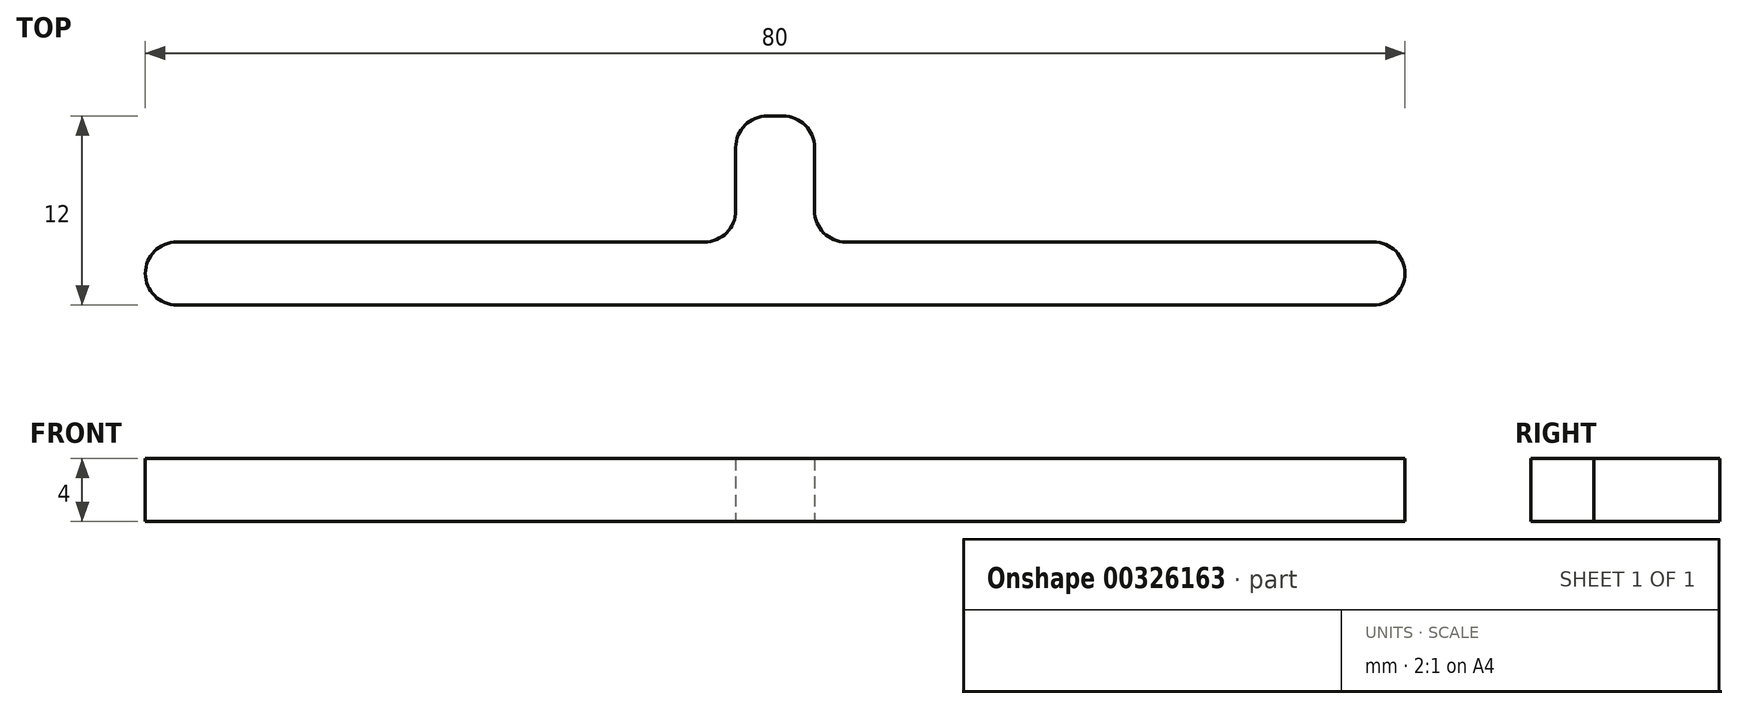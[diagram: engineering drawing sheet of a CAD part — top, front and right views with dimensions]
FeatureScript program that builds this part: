
annotation { "Feature Type Name" : "Feature", "Feature Type Description" : "" }
export const myFeature = defineFeature(function(context is Context, id is Id, definition is map)
    precondition{}
    {
        {
            var Q0;
            Q0=qCreatedBy(makeId("Top.planeOp"),FACE);
            var sketch = newSketch(context, id + "F0", { "sketchPlane" : qUnion([Q0])});
            skLineSegment(sketch, "E0.bottom", {"start": v(-40, 2) * mm, "end": v(40, 2) * mm});
            skLineSegment(sketch, "E0.top", {"start": v(-40, -2) * mm, "end": v(40, -2) * mm});
            skLineSegment(sketch, "E0.left", {"start": v(-40, 2) * mm, "end": v(-40, -2) * mm});
            skLineSegment(sketch, "E0.right", {"start": v(40, 2) * mm, "end": v(40, -2) * mm});
            skPoint(sketch, "E0.middle", {"position": v(0, 0) * mm});
            skLineSegment(sketch, "E1.bottom", {"start": v(-2.5, 2) * mm, "end": v(2.5, 2) * mm});
            skLineSegment(sketch, "E1.top", {"start": v(-2.5, 10) * mm, "end": v(2.5, 10) * mm});
            skLineSegment(sketch, "E1.left", {"start": v(-2.5, 2) * mm, "end": v(-2.5, 10) * mm});
            skLineSegment(sketch, "E1.right", {"start": v(2.5, 2) * mm, "end": v(2.5, 10) * mm});
            skPoint(sketch, "E1.middle", {"position": v(0, 6) * mm});
            skSolve(sketch);
        }
        {
            var Q0;
            Q0 = qSketchRegion(id + "F0", true);
            extrude(context, id + "F1", {"entities" : qUnion([Q0]), "depth" : 4 * mm});
        }
        {
            var Q0;
            Q0=makeQuery(id+"F1.opExtrude","SWEPT_EDGE",EDGE,{"disambiguationData":[OSD([sQuery(id+"F0.wireOp",EDGE,"E0.top"),sQuery(id+"F0.wireOp",EDGE,"E0.left")])]});
            var Q1;
            Q1=makeQuery(id+"F1.opExtrude","SWEPT_EDGE",EDGE,{"disambiguationData":[OSD([sQuery(id+"F0.wireOp",EDGE,"E0.top"),sQuery(id+"F0.wireOp",EDGE,"E0.right")])]});
            var Q2;
            Q2=makeQuery(id+"F1.opExtrude","SWEPT_EDGE",EDGE,{"disambiguationData":[OSD([sQuery(id+"F0.wireOp",EDGE,"E0.bottom"),sQuery(id+"F0.wireOp",EDGE,"E0.right")])]});
            var Q3;
            Q3=makeQuery(id+"F1.opExtrude","SWEPT_EDGE",EDGE,{"disambiguationData":[OSD([sQuery(id+"F0.wireOp",EDGE,"E0.bottom"),sQuery(id+"F0.wireOp",EDGE,"E0.left")])]});
            var Q4;
            Q4=makeQuery(id+"F1.opExtrude","SWEPT_EDGE",EDGE,{"disambiguationData":[OSD([sQuery(id+"F0.wireOp",EDGE,"E1.top"),sQuery(id+"F0.wireOp",EDGE,"E1.left")])]});
            var Q5;
            Q5=makeQuery(id+"F1.opExtrude","SWEPT_EDGE",EDGE,{"disambiguationData":[OSD([sQuery(id+"F0.wireOp",EDGE,"E1.top"),sQuery(id+"F0.wireOp",EDGE,"E1.right")])]});
            var Q6;
            Q6=makeQuery(id+"F1.opExtrude","SWEPT_EDGE",EDGE,{"disambiguationData":[OSD([sQuery(id+"F0.wireOp",EDGE,"E0.bottom"),sQuery(id+"F0.wireOp",EDGE,"E1.bottom"),sQuery(id+"F0.wireOp",EDGE,"E1.left")])]});
            var Q7;
            Q7=makeQuery(id+"F1.opExtrude","SWEPT_EDGE",EDGE,{"disambiguationData":[OSD([sQuery(id+"F0.wireOp",EDGE,"E0.bottom"),sQuery(id+"F0.wireOp",EDGE,"E1.bottom"),sQuery(id+"F0.wireOp",EDGE,"E1.right")])]});
            fillet(context, id + "F2", {"entities" : qUnion([Q0, Q1, Q2, Q3, Q4, Q5, Q6, Q7]), "radius" : 2 * mm, "tangentPropagation" : true, "allowEdgeOverflow" : false});
        }
    });
